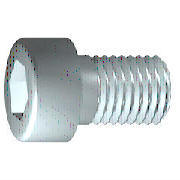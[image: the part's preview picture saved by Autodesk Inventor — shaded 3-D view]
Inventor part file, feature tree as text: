
AUTODESK INVENTOR PART (.ipt)
format: ipt  version: 2017 (Build 210142000, 142)  size: 192,512 bytes
history: native  units: mm (DEFAULTED — no unit token found)
features: sketch x2, other x1, extrude x1, plane x1, fillet x1
ambient origin geometry x7: Origin, YZ Plane, XY Plane, X Axis, Y Axis, Z Axis, Center Point
bodies: Solid1 (feature_tree)
feature tree (6):
  other  "Corps"
  extrude  "Rainure"  Depth=8.75mm
  plane  "Work Plane1"
  fillet  "Fillet2"  Radius=0.306825mm
  sketch  "Esquisse1"
  sketch  "Esquisse2"
